# Revit family: NBS_Senator_OffcChrs_Freeflex-en-us
name_source: partatom
category: Furniture
revit_build: Autodesk Revit 2016 (Build: 20151007_0715(x64)
units: mm (PartAtom-declared; Revit-internal decimal feet)

## family parameters
Always vertical = Yes
Cut with Voids When Loaded = No
Room Calculation Point = No
Shared = No
Work Plane-Based = No

## types (2) — shared parameters
Adjustability = Up to 22° of recline motion, back lock, seat depth, height adjustable, multi-adjustable arms
AssetType = Moveable
BaseFinishes = Graphite plastic, polished aluminium
Category = Pr_40_50_12_57:Office chairs
CodePerformance = ANSI/BIFMA X5.1-2011
Depth = 27 "
DurationUnit = year
ExpectedLife = 10
Features = Graphite plastic base, 2.5" hard wheel castors, graphite gas lift, graphite components (with optional black or light grey back and arms), weight controlled synchronized mechanism with travel limitation in 4 steps including locking upright, 2.75"  back height adjustment, integrated flexible back membrane, 2.4" seat depth adjustment, contrasting mesh side panels on seat and back - storm, carbon, fog, aqua, avocado or sunset: complementary colored back insert - brushed, storm, carbon, fog, aqua, avocado or sunset, molded seat and back foam, user instructions
Finish = 5 star base available in graphite plastic or polished aluminium, plastic components available in graphite with black or light grey back and arms, contrasting mesh side panels and back inserts available in either fog, cardon, storm, sunset, aqua or avacado, freeflex can be upholstered in a broad range of contract upholstery fabrics, vinyls and leathers from senator standard upholstery collection
FinishOptions = 5 Star base available in graphite plastic or polished aluminium, plastic components available in graphite with black or light grey back and arms, contrasting mesh side panels and back inserts available in either Fog, Cardon, Storm, Sunset, Aqua or Avacado, freeflex can be upholstered in a broad range of contract upholstery fabrics, vinyls and leathers from senator standard upholstery collection
FrameMountingMaterial = NBS_Concept
HighestSeatingHeight = 22 "
IfcExportAs = IfcFurnitureType
IfcExportType = CHAIR
IsBuiltIn = No
LegHeight = 15 "
LowestSeatingHeight = 18 "
ManufacturerName = Senator
ManufacturerURL = http://www.thesenatorgroup.com
MeshSidePanelColours = Fog, carbon, storm, sunset, aqua, avocado
NBSCertification = www.nationalbimlibrary.com/cert/x2az4lco
NBSDescription = Office chairs
NBSReference = 45-35-20/330
NominalDepth = 27 "
NominalLength = 27 "
NominalWidth = 27 "
OfficeChairBase = NBS_TheSenatorGroup_OfficeChairs_Freeflex-5StarBaseWCastors
OfficeChairMechanism = NBS_TheSenatorGroup_OfficeChairs_Freeflex_TiltMechanism
OfficeChairSeat = NBS_TheSenatorGroup_OfficeChairs_Freeflex_Seat
OmniClassCode = 22-12 52 23
OmniClassTitle = Office Seating
OmniClassVersion = Table 22 2012-05-16
ProductInformation = http://www.thesenatorgroup.com
SeatArmMaterial = NBS_Concept
SeatBaseMaterial = NBS_Concept
SeatFrameMaterial = NBS_Concept
SeatTiltMaterial = NBS_Concept
SeatTrimMaterial = NBS_Concept
SeatingHeight = 20 "
SeatingSeatMaterial = NBS_Concept
SeatsAndBacksColourOptions = Fog, carbon, storm, sunset, aqua, avocado, brushed
StandardsDimensions = ANSI/BIFMA X5.1-2011
StandardsDurability = ANSI/BIFMA X5.1-2011
StandardsSafetyRequirements = ANSI/BIFMA X5.1-2011
Status = UNSET
SustainabilityPerformance = 100% recycleable
Uniclass2015Code = Pr_40_50_12_57
Uniclass2015Title = Office chairs
Uniclass2015Version = Products v1.10
Version = 1
WarrantyDescription = Senator warrants that its manufactured products are free from manufacturing defects - in materials or workmanship - for a period of ten (10) years on Senator Seating ranges; and fifteen (15) years on Senator Desking ranges
WarrantyDurationParts = 10
WarrantyDurationUnit = year
Width = 27 "
zero-valued in all types: FootHeight, NominalHeight

## per-type parameters (varying)
| type | BIMObjectName | Description | HasArms | ModelReference | Name |
| FLX740 | NBS_Senator_OfficeChairs_Freeflex_FLX740-US | Task chair with no arms | No | Freeflex | OfficeChairs_Freeflex_FLX740-US_Senator |
| FLX740HA | NBS_Senator_OfficeChairs_Freeflex_FLX740HA-US | Task chair with heiaght and width adjustable arms | Yes | Freeflex with arms | OfficeChairs_Freeflex_FLX740HA-US_Senator |

note: column(s) folded — value = type name in every type: ModelNumber

## geometry (parser evidence)
native form markers: Sweep x14
no freeform markers — native parametric forms only
